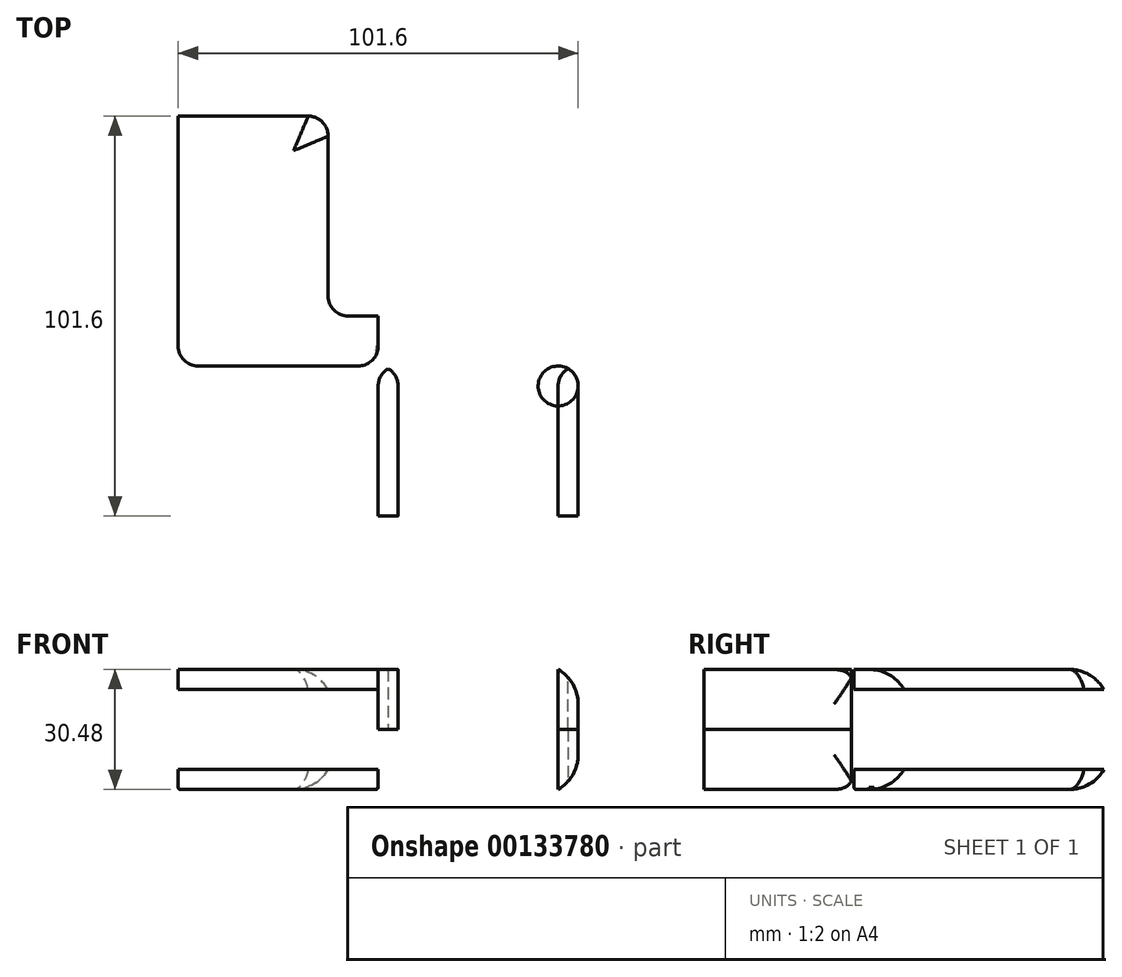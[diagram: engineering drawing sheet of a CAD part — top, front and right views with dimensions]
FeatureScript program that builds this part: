
annotation { "Feature Type Name" : "Feature", "Feature Type Description" : "" }
export const myFeature = defineFeature(function(context is Context, id is Id, definition is map)
    precondition{}
    {
        {
            var Q0;
            Q0=qCreatedBy(makeId("Top.planeOp"),FACE);
            var sketch = newSketch(context, id + "F0", { "sketchPlane" : qUnion([Q0])});
            skLineSegment(sketch, "E0.bottom", {"start": v(0, 0) * mm, "end": v(38.1, 0) * mm});
            skLineSegment(sketch, "E0.top", {"start": v(0, 101.6) * mm, "end": v(38.1, 101.6) * mm});
            skLineSegment(sketch, "E0.left", {"start": v(0, 0) * mm, "end": v(0, 101.6) * mm});
            skLineSegment(sketch, "E0.right", {"start": v(38.1, 0) * mm, "end": v(38.1, 101.6) * mm});
            skLineSegment(sketch, "E1.bottom", {"start": v(0, 0) * mm, "end": v(101.6, 0) * mm});
            skLineSegment(sketch, "E1.top", {"start": v(0, 38.1) * mm, "end": v(101.6, 38.1) * mm});
            skLineSegment(sketch, "E1.left", {"start": v(0, 0) * mm, "end": v(0, 38.1) * mm});
            skLineSegment(sketch, "E1.right", {"start": v(101.6, 0) * mm, "end": v(101.6, 38.1) * mm});
            skLineSegment(sketch, "E2.bottom", {"start": v(0, 0) * mm, "end": v(50.8, 0) * mm});
            skLineSegment(sketch, "E2.top", {"start": v(0, 50.8) * mm, "end": v(50.8, 50.8) * mm});
            skLineSegment(sketch, "E2.left", {"start": v(0, 0) * mm, "end": v(0, 50.8) * mm});
            skLineSegment(sketch, "E2.right", {"start": v(50.8, 0) * mm, "end": v(50.8, 50.8) * mm});
            skLineSegment(sketch, "E3.bottom", {"start": v(0, 96.52) * mm, "end": v(38.1, 96.52) * mm});
            skLineSegment(sketch, "E3.top", {"start": v(0, 55.88) * mm, "end": v(38.1, 55.88) * mm});
            skLineSegment(sketch, "E3.left", {"start": v(0, 96.52) * mm, "end": v(0, 55.88) * mm});
            skLineSegment(sketch, "E3.right", {"start": v(38.1, 96.52) * mm, "end": v(38.1, 55.88) * mm});
            skLineSegment(sketch, "E4.bottom", {"start": v(96.52, 38.1) * mm, "end": v(55.88, 38.1) * mm});
            skLineSegment(sketch, "E4.top", {"start": v(96.52, 0) * mm, "end": v(55.88, 0) * mm});
            skLineSegment(sketch, "E4.left", {"start": v(96.52, 38.1) * mm, "end": v(96.52, 0) * mm});
            skLineSegment(sketch, "E4.right", {"start": v(55.88, 38.1) * mm, "end": v(55.88, 0) * mm});
            skSolve(sketch);
        }
        {
            var Q0;
            {var subQ0=sQuery(id+"F0.wireOp",EDGE,"E0.top");Q0=makeQuery(id+"F0.imprint","IMPRINT",FACE,{"disambiguationData":[TD([[makeQuery(id+"F0.imprint","IMPRINT",EDGE,{"derivedFrom":subQ0}),-1.0]])]});}
            var Q1;
            Q1=makeQuery(id+"F0.imprint","IMPRINT",FACE,{"disambiguationData":[TD([[makeQuery(id+"F0.imprint","IMPRINT",EDGE,{"derivedFrom":sQuery(id+"F0.wireOp",EDGE,"E3.bottom")}),-1.0]])]});
            var Q2;
            {var subQ3=sQuery(id+"F0.wireOp",EDGE,"E3.top");Q2=makeQuery(id+"F0.imprint","IMPRINT",FACE,{"disambiguationData":[TD([[makeQuery(id+"F0.imprint","IMPRINT",EDGE,{"derivedFrom":subQ3}),-1.0]])]});}
            var Q3;
            {var subQ0=sQuery(id+"F0.wireOp",EDGE,"E2.top");var subQ1=sQuery(id+"F0.wireOp",EDGE,"E0.right");var subQ2=makeQuery(id+"F0.imprint","INTERSECT",VERTEX,{"derivedFrom":[subQ1,subQ0]});Q3=makeQuery(id+"F0.imprint","IMPRINT",FACE,{"disambiguationData":[TD([[makeQuery(id+"F0.imprint","IMPRINT",EDGE,{"disambiguationData":[TD([[subQ2,1.0]])],"derivedFrom":subQ1}),1.0]])]});}
            var Q4;
            {var subQ0=sQuery(id+"F0.wireOp",EDGE,"E2.bottom");var subQ1=sQuery(id+"F0.wireOp",EDGE,"E0.right");var subQ2=makeQuery(id+"F0.imprint","INTERSECT",VERTEX,{"derivedFrom":[subQ1,subQ0]});Q4=makeQuery(id+"F0.imprint","IMPRINT",FACE,{"disambiguationData":[TD([[makeQuery(id+"F0.imprint","IMPRINT",EDGE,{"disambiguationData":[TD([[subQ2,-1.0]])],"derivedFrom":subQ1}),1.0]])]});}
            var Q5;
            {var subQ0=sQuery(id+"F0.wireOp",EDGE,"E2.bottom");var subQ1=sQuery(id+"F0.wireOp",EDGE,"E0.right");var subQ2=makeQuery(id+"F0.imprint","INTERSECT",VERTEX,{"derivedFrom":[subQ1,subQ0]});Q5=makeQuery(id+"F0.imprint","IMPRINT",FACE,{"disambiguationData":[TD([[makeQuery(id+"F0.imprint","IMPRINT",EDGE,{"disambiguationData":[TD([[subQ2,-1.0]])],"derivedFrom":subQ1}),-1.0]])]});}
            var Q6;
            {var subQ3=sQuery(id+"F0.wireOp",EDGE,"E4.right");Q6=makeQuery(id+"F0.imprint","IMPRINT",FACE,{"disambiguationData":[TD([[makeQuery(id+"F0.imprint","IMPRINT",EDGE,{"derivedFrom":subQ3}),-1.0]])]});}
            var Q7;
            Q7=makeQuery(id+"F0.imprint","IMPRINT",FACE,{"disambiguationData":[TD([[makeQuery(id+"F0.imprint","IMPRINT",EDGE,{"derivedFrom":sQuery(id+"F0.wireOp",EDGE,"E4.bottom")}),1.0]])]});
            var Q8;
            {var subQ0=sQuery(id+"F0.wireOp",EDGE,"E1.right");Q8=makeQuery(id+"F0.imprint","IMPRINT",FACE,{"disambiguationData":[TD([[makeQuery(id+"F0.imprint","IMPRINT",EDGE,{"derivedFrom":subQ0}),1.0]])]});}
            extrude(context, id + "F1", {"entities" : qUnion([Q0, Q1, Q2, Q3, Q4, Q5, Q6, Q7, Q8]), "depth" : 15.24 * mm});
        }
        {
            var Q0;
            Q0=makeQuery(id+"F0.imprint","IMPRINT",FACE,{"disambiguationData":[TD([[makeQuery(id+"F0.imprint","IMPRINT",EDGE,{"derivedFrom":sQuery(id+"F0.wireOp",EDGE,"E3.bottom")}),-1.0]])]});
            var Q1;
            {var subQ0=sQuery(id+"F0.wireOp",EDGE,"E2.top");var subQ1=sQuery(id+"F0.wireOp",EDGE,"E0.right");var subQ2=makeQuery(id+"F0.imprint","INTERSECT",VERTEX,{"derivedFrom":[subQ1,subQ0]});Q1=makeQuery(id+"F0.imprint","IMPRINT",FACE,{"disambiguationData":[TD([[makeQuery(id+"F0.imprint","IMPRINT",EDGE,{"disambiguationData":[TD([[subQ2,1.0]])],"derivedFrom":subQ1}),1.0]])]});}
            var Q2;
            {var subQ0=sQuery(id+"F0.wireOp",EDGE,"E2.bottom");var subQ1=sQuery(id+"F0.wireOp",EDGE,"E0.right");var subQ2=makeQuery(id+"F0.imprint","INTERSECT",VERTEX,{"derivedFrom":[subQ1,subQ0]});Q2=makeQuery(id+"F0.imprint","IMPRINT",FACE,{"disambiguationData":[TD([[makeQuery(id+"F0.imprint","IMPRINT",EDGE,{"disambiguationData":[TD([[subQ2,-1.0]])],"derivedFrom":subQ1}),1.0]])]});}
            var Q3;
            {var subQ0=sQuery(id+"F0.wireOp",EDGE,"E2.bottom");var subQ1=sQuery(id+"F0.wireOp",EDGE,"E0.right");var subQ2=makeQuery(id+"F0.imprint","INTERSECT",VERTEX,{"derivedFrom":[subQ1,subQ0]});Q3=makeQuery(id+"F0.imprint","IMPRINT",FACE,{"disambiguationData":[TD([[makeQuery(id+"F0.imprint","IMPRINT",EDGE,{"disambiguationData":[TD([[subQ2,-1.0]])],"derivedFrom":subQ1}),-1.0]])]});}
            var Q4;
            Q4=makeQuery(id+"F0.imprint","IMPRINT",FACE,{"disambiguationData":[TD([[makeQuery(id+"F0.imprint","IMPRINT",EDGE,{"derivedFrom":sQuery(id+"F0.wireOp",EDGE,"E4.bottom")}),1.0]])]});
            extrude(context, id + "F2", {"entities" : qUnion([Q0, Q1, Q2, Q3, Q4]), "operationType" : NewBodyOperationType.REMOVE, "depth" : 10.16 * mm});
        }
        {
            var Q0;
            Q0=makeQuery(id+"F1.opExtrude","SWEPT_BODY",BODY,{"disambiguationData":[OSD([sQuery(id+"F0.wireOp",EDGE,"E0.top"),sQuery(id+"F0.wireOp",EDGE,"E0.left"),sQuery(id+"F0.wireOp",EDGE,"E0.right"),sQuery(id+"F0.wireOp",EDGE,"E1.bottom"),sQuery(id+"F0.wireOp",EDGE,"E1.top"),sQuery(id+"F0.wireOp",EDGE,"E1.right"),sQuery(id+"F0.wireOp",EDGE,"E2.bottom"),sQuery(id+"F0.wireOp",EDGE,"E2.left"),sQuery(id+"F0.wireOp",EDGE,"E3.left"),sQuery(id+"F0.wireOp",EDGE,"E3.right"),sQuery(id+"F0.wireOp",EDGE,"E4.bottom"),sQuery(id+"F0.wireOp",EDGE,"E4.top")])]});
            var Q1;
            Q1=qCreatedBy(makeId("Top.planeOp"),FACE);
            mirror(context, id + "F3", {"operationType" : NewBodyOperationType.ADD, "entities" : qUnion([Q0]), "mirrorPlane" : qUnion([Q1])});
        }
        {
            var Q0;
            Q0=makeQuery(id+"F2.boolean.opBoolean","COPY",EDGE,{"derivedFrom":makeQuery(id+"F2.opExtrude","CAP_EDGE",EDGE,{"disambiguationData":[OSD([sQuery(id+"F0.wireOp",EDGE,"E3.bottom")])],"isStart":false})});
            var Q1;
            Q1=makeQuery(id+"F3.opPattern","COPY",EDGE,{"derivedFrom":makeQuery(id+"F2.boolean.opBoolean","COPY",EDGE,{"derivedFrom":makeQuery(id+"F2.opExtrude","CAP_EDGE",EDGE,{"disambiguationData":[OSD([sQuery(id+"F0.wireOp",EDGE,"E3.bottom")])],"isStart":false})}),"instanceName":"1"});
            var Q2;
            Q2=makeQuery(id+"F3.opPattern","COPY",EDGE,{"derivedFrom":makeQuery(id+"F2.boolean.opBoolean","COPY",EDGE,{"derivedFrom":makeQuery(id+"F2.opExtrude","CAP_EDGE",EDGE,{"disambiguationData":[OSD([sQuery(id+"F0.wireOp",EDGE,"E3.top")])],"isStart":false})}),"instanceName":"1"});
            var Q3;
            Q3=makeQuery(id+"F3.opPattern","COPY",EDGE,{"derivedFrom":makeQuery(id+"F2.boolean.opBoolean","COPY",EDGE,{"derivedFrom":makeQuery(id+"F2.opExtrude","CAP_EDGE",EDGE,{"disambiguationData":[OSD([sQuery(id+"F0.wireOp",EDGE,"E2.top")])],"isStart":false})}),"instanceName":"1"});
            var Q4;
            Q4=makeQuery(id+"F2.boolean.opBoolean","COPY",EDGE,{"derivedFrom":makeQuery(id+"F2.opExtrude","CAP_EDGE",EDGE,{"disambiguationData":[OSD([sQuery(id+"F0.wireOp",EDGE,"E3.top")])],"isStart":false})});
            var Q5;
            Q5=makeQuery(id+"F2.boolean.opBoolean","COPY",EDGE,{"derivedFrom":makeQuery(id+"F2.opExtrude","CAP_EDGE",EDGE,{"disambiguationData":[OSD([sQuery(id+"F0.wireOp",EDGE,"E2.top")])],"isStart":false})});
            var Q6;
            Q6=makeQuery(id+"F2.boolean.opBoolean","COPY",EDGE,{"derivedFrom":makeQuery(id+"F2.opExtrude","CAP_EDGE",EDGE,{"disambiguationData":[OSD([sQuery(id+"F0.wireOp",EDGE,"E2.right")])],"isStart":false})});
            var Q7;
            Q7=makeQuery(id+"F3.opPattern","COPY",EDGE,{"derivedFrom":makeQuery(id+"F2.boolean.opBoolean","COPY",EDGE,{"derivedFrom":makeQuery(id+"F2.opExtrude","CAP_EDGE",EDGE,{"disambiguationData":[OSD([sQuery(id+"F0.wireOp",EDGE,"E2.right")])],"isStart":false})}),"instanceName":"1"});
            var Q8;
            Q8=makeQuery(id+"F3.opPattern","COPY",EDGE,{"derivedFrom":makeQuery(id+"F2.boolean.opBoolean","COPY",EDGE,{"derivedFrom":makeQuery(id+"F2.opExtrude","CAP_EDGE",EDGE,{"disambiguationData":[OSD([sQuery(id+"F0.wireOp",EDGE,"E4.left")])],"isStart":false})}),"instanceName":"1"});
            var Q9;
            Q9=makeQuery(id+"F2.boolean.opBoolean","COPY",EDGE,{"derivedFrom":makeQuery(id+"F2.opExtrude","CAP_EDGE",EDGE,{"disambiguationData":[OSD([sQuery(id+"F0.wireOp",EDGE,"E4.left")])],"isStart":false})});
            var Q10;
            Q10=makeQuery(id+"F2.boolean.opBoolean","COPY",EDGE,{"derivedFrom":makeQuery(id+"F2.opExtrude","CAP_EDGE",EDGE,{"disambiguationData":[OSD([sQuery(id+"F0.wireOp",EDGE,"E4.right")])],"isStart":false})});
            var Q11;
            Q11=makeQuery(id+"F3.opPattern","COPY",EDGE,{"derivedFrom":makeQuery(id+"F2.boolean.opBoolean","COPY",EDGE,{"derivedFrom":makeQuery(id+"F2.opExtrude","CAP_EDGE",EDGE,{"disambiguationData":[OSD([sQuery(id+"F0.wireOp",EDGE,"E4.right")])],"isStart":false})}),"instanceName":"1"});
            var Q12;
            Q12=makeQuery(id+"F1.opExtrude","SWEPT_EDGE",EDGE,{"disambiguationData":[OSD([sQuery(id+"F0.wireOp",EDGE,"E0.right"),sQuery(id+"F0.wireOp",EDGE,"E1.top")])]});
            var Q13;
            Q13=makeQuery(id+"F3.opPattern","COPY",EDGE,{"derivedFrom":makeQuery(id+"F1.opExtrude","SWEPT_EDGE",EDGE,{"disambiguationData":[OSD([sQuery(id+"F0.wireOp",EDGE,"E0.right"),sQuery(id+"F0.wireOp",EDGE,"E1.top")])]}),"instanceName":"1"});
            fillet(context, id + "F4", {"entities" : qUnion([Q0, Q1, Q2, Q3, Q4, Q5, Q6, Q7, Q8, Q9, Q10, Q11, Q12, Q13]), "radius" : 5.08 * mm, "tangentPropagation" : true, "allowEdgeOverflow" : false});
        }
        {
            var Q0;
            Q0=makeQuery(id+"F1.opExtrude","SWEPT_EDGE",EDGE,{"disambiguationData":[OSD([sQuery(id+"F0.wireOp",EDGE,"E2.bottom"),sQuery(id+"F0.wireOp",EDGE,"E2.left")])]});
            var Q1;
            Q1=makeQuery(id+"F3.opPattern","COPY",EDGE,{"derivedFrom":makeQuery(id+"F1.opExtrude","SWEPT_EDGE",EDGE,{"disambiguationData":[OSD([sQuery(id+"F0.wireOp",EDGE,"E2.bottom"),sQuery(id+"F0.wireOp",EDGE,"E2.left")])]}),"instanceName":"1"});
            var Q2;
            Q2=makeQuery(id+"F1.opExtrude","CAP_EDGE",EDGE,{"disambiguationData":[OSD([sQuery(id+"F0.wireOp",EDGE,"E0.top")])],"isStart":false});
            var Q3;
            Q3=makeQuery(id+"F3.opPattern","COPY",EDGE,{"derivedFrom":makeQuery(id+"F1.opExtrude","CAP_EDGE",EDGE,{"disambiguationData":[OSD([sQuery(id+"F0.wireOp",EDGE,"E0.top")])],"isStart":false}),"instanceName":"1"});
            var Q4;
            Q4=makeQuery(id+"F1.opExtrude","CAP_EDGE",EDGE,{"disambiguationData":[OSD([sQuery(id+"F0.wireOp",EDGE,"E1.right")])],"isStart":false});
            var Q5;
            Q5=makeQuery(id+"F3.opPattern","COPY",EDGE,{"derivedFrom":makeQuery(id+"F1.opExtrude","CAP_EDGE",EDGE,{"disambiguationData":[OSD([sQuery(id+"F0.wireOp",EDGE,"E1.right")])],"isStart":false}),"instanceName":"1"});
            fillet(context, id + "F5", {"entities" : qUnion([Q0, Q1, Q2, Q3, Q4, Q5]), "radius" : 10.16 * mm, "tangentPropagation" : true, "allowEdgeOverflow" : false});
        }
        {
            var Q0;
            Q0=makeQuery(id+"F1.opExtrude","CAP_EDGE",EDGE,{"disambiguationData":[OSD([sQuery(id+"F0.wireOp",EDGE,"E1.bottom"),sQuery(id+"F0.wireOp",EDGE,"E2.bottom"),sQuery(id+"F0.wireOp",EDGE,"E4.top")])],"isStart":false});
            var Q1;
            Q1=makeQuery(id+"F3.opPattern","COPY",EDGE,{"derivedFrom":makeQuery(id+"F2.boolean.opBoolean","COPY",EDGE,{"derivedFrom":makeQuery(id+"F2.opExtrude","CAP_EDGE",EDGE,{"disambiguationData":[OSD([sQuery(id+"F0.wireOp",EDGE,"E2.bottom")])],"isStart":false})}),"instanceName":"1"});
            var Q2;
            Q2=makeQuery(id+"F3.opPattern","COPY",EDGE,{"derivedFrom":makeQuery(id+"F1.opExtrude","CAP_EDGE",EDGE,{"disambiguationData":[OSD([sQuery(id+"F0.wireOp",EDGE,"E1.bottom"),sQuery(id+"F0.wireOp",EDGE,"E2.bottom"),sQuery(id+"F0.wireOp",EDGE,"E4.top")])],"isStart":false}),"instanceName":"1"});
            var Q3;
            Q3=makeQuery(id+"F3.opPattern","COPY",EDGE,{"derivedFrom":makeQuery(id+"F2.boolean.opBoolean","COPY",EDGE,{"derivedFrom":makeQuery(id+"F2.opExtrude","CAP_EDGE",EDGE,{"disambiguationData":[OSD([sQuery(id+"F0.wireOp",EDGE,"E4.top")])],"isStart":false})}),"instanceName":"1"});
            var Q4;
            Q4=makeQuery(id+"F3.opPattern","COPY",EDGE,{"derivedFrom":makeQuery(id+"F2.boolean.opBoolean","COPY",EDGE,{"derivedFrom":makeQuery(id+"F2.opExtrude","CAP_EDGE",EDGE,{"disambiguationData":[OSD([sQuery(id+"F0.wireOp",EDGE,"E4.bottom")])],"isStart":false})}),"instanceName":"1"});
            var Q5;
            {var subQ0=sQuery(id+"F0.wireOp",EDGE,"E1.top");var subQ1=sQuery(id+"F0.wireOp",EDGE,"E0.right");Q5=makeQuery(id+"F4.opFillet","BLEND_EDGE",EDGE,{"blendedFrom":[makeQuery(id+"F3.opPattern","COPY",EDGE,{"derivedFrom":makeQuery(id+"F1.opExtrude","SWEPT_EDGE",EDGE,{"disambiguationData":[OSD([subQ1,subQ0])]}),"instanceName":"1"}),makeQuery(id+"F3.opPattern","COPY",FACE,{"derivedFrom":makeQuery(id+"F2.boolean.opBoolean","COPY",FACE,{"derivedFrom":makeQuery(id+"F2.opExtrude","CAP_FACE",FACE,{"disambiguationData":[OSD([subQ1,subQ0,sQuery(id+"F0.wireOp",EDGE,"E2.bottom"),sQuery(id+"F0.wireOp",EDGE,"E2.top"),sQuery(id+"F0.wireOp",EDGE,"E2.left"),sQuery(id+"F0.wireOp",EDGE,"E2.right")])],"isStart":false})}),"instanceName":"1"})],"blendedInto":[makeQuery(id+"F3.opPattern","COPY",FACE,{"derivedFrom":makeQuery(id+"F2.boolean.opBoolean","COPY",FACE,{"derivedFrom":makeQuery(id+"F2.opExtrude","CAP_FACE",FACE,{"disambiguationData":[OSD([subQ1,subQ0,sQuery(id+"F0.wireOp",EDGE,"E2.bottom"),sQuery(id+"F0.wireOp",EDGE,"E2.top"),sQuery(id+"F0.wireOp",EDGE,"E2.left"),sQuery(id+"F0.wireOp",EDGE,"E2.right")])],"isStart":false})}),"instanceName":"1"})]});}
            var Q6;
            Q6=makeQuery(id+"F3.opPattern","COPY",EDGE,{"derivedFrom":makeQuery(id+"F1.opExtrude","CAP_EDGE",EDGE,{"disambiguationData":[OSD([sQuery(id+"F0.wireOp",EDGE,"E1.top"),sQuery(id+"F0.wireOp",EDGE,"E4.bottom")])],"isStart":false}),"instanceName":"1"});
            var Q7;
            Q7=makeQuery(id+"F3.opPattern","COPY",EDGE,{"derivedFrom":makeQuery(id+"F2.boolean.opBoolean","COPY",EDGE,{"derivedFrom":makeQuery(id+"F2.opExtrude","CAP_EDGE",EDGE,{"disambiguationData":[OSD([sQuery(id+"F0.wireOp",EDGE,"E3.right")])],"isStart":false})}),"instanceName":"1"});
            var Q8;
            Q8=makeQuery(id+"F3.opPattern","COPY",EDGE,{"derivedFrom":makeQuery(id+"F2.boolean.opBoolean","COPY",EDGE,{"derivedFrom":makeQuery(id+"F2.opExtrude","CAP_EDGE",EDGE,{"disambiguationData":[OSD([sQuery(id+"F0.wireOp",EDGE,"E3.left")])],"isStart":false})}),"instanceName":"1"});
            fillet(context, id + "F6", {"entities" : qUnion([Q0, Q1, Q2, Q3, Q4, Q5, Q6, Q7, Q8]), "radius" : 0.5 * mm, "tangentPropagation" : true, "allowEdgeOverflow" : false});
        }
    });
